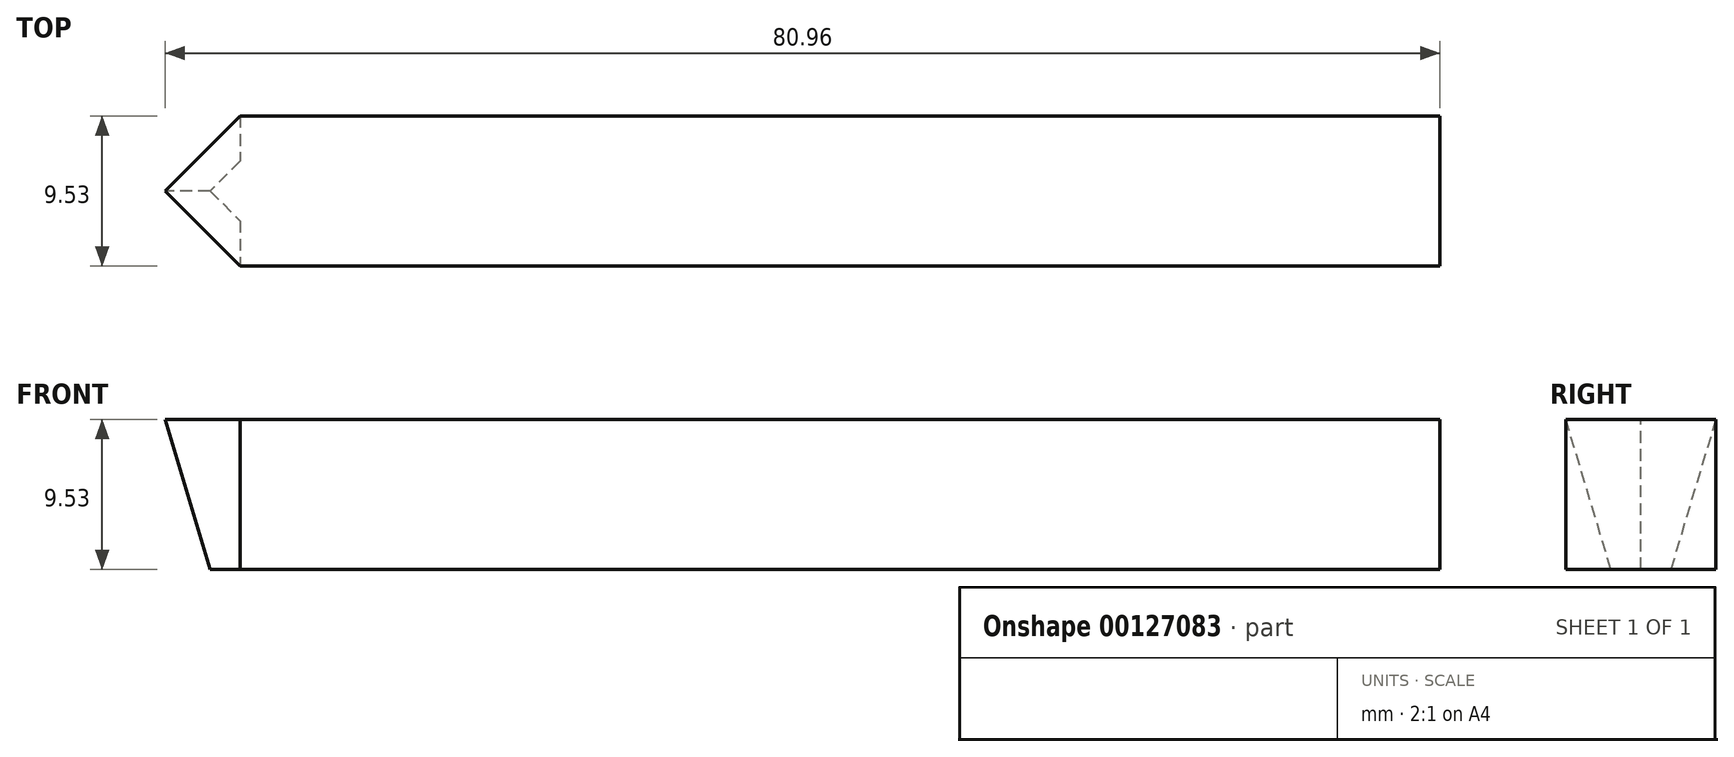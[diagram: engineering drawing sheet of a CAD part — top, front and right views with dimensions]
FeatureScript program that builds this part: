
annotation { "Feature Type Name" : "Feature", "Feature Type Description" : "" }
export const myFeature = defineFeature(function(context is Context, id is Id, definition is map)
    precondition{}
    {
        {
            var Q0;
            Q0=qCreatedBy(makeId("Top.planeOp"),FACE);
            var sketch = newSketch(context, id + "F0", { "sketchPlane" : qUnion([Q0])});
            skLineSegment(sketch, "E0.bottom", {"start": v(0, 0) * mm, "end": v(76.2, 0) * mm});
            skLineSegment(sketch, "E0.top", {"start": v(0, -9.53) * mm, "end": v(76.2, -9.53) * mm});
            skLineSegment(sketch, "E0.left", {"start": v(0, 0) * mm, "end": v(0, -9.52) * mm});
            skLineSegment(sketch, "E0.right", {"start": v(76.2, 0) * mm, "end": v(76.2, -9.53) * mm});
            skLineSegment(sketch, "E1", {"start": v(0, 0) * mm, "end": v(-4.76, -4.76) * mm});
            skPoint(sketch, "E1.endSnap0", {"position": v(0, -4.76) * mm});
            skLineSegment(sketch, "E2", {"start": v(-4.76, -4.76) * mm, "end": v(0, -9.53) * mm});
            skSolve(sketch);
        }
        {
            var Q0;
            Q0=makeQuery(id+"F0.imprint","IMPRINT",FACE,{"disambiguationData":[TD([[makeQuery(id+"F0.imprint","IMPRINT",EDGE,{"derivedFrom":sQuery(id+"F0.wireOp",EDGE,"E0.bottom")}),-1.0]])]});
            extrude(context, id + "F1", {"entities" : qUnion([Q0]), "oppositeDirection" : true, "depth" : 9.52 * mm});
        }
        {
            var Q0;
            Q0 = qSketchRegion(id + "F0", true);
            extrude(context, id + "F2", {"entities" : qUnion([Q0]), "operationType" : NewBodyOperationType.ADD, "oppositeDirection" : true, "depth" : 9.52 * mm, "hasDraft" : true, "draftAngle" : 12 * degree, "draftPullDirection" : true});
        }
    });
